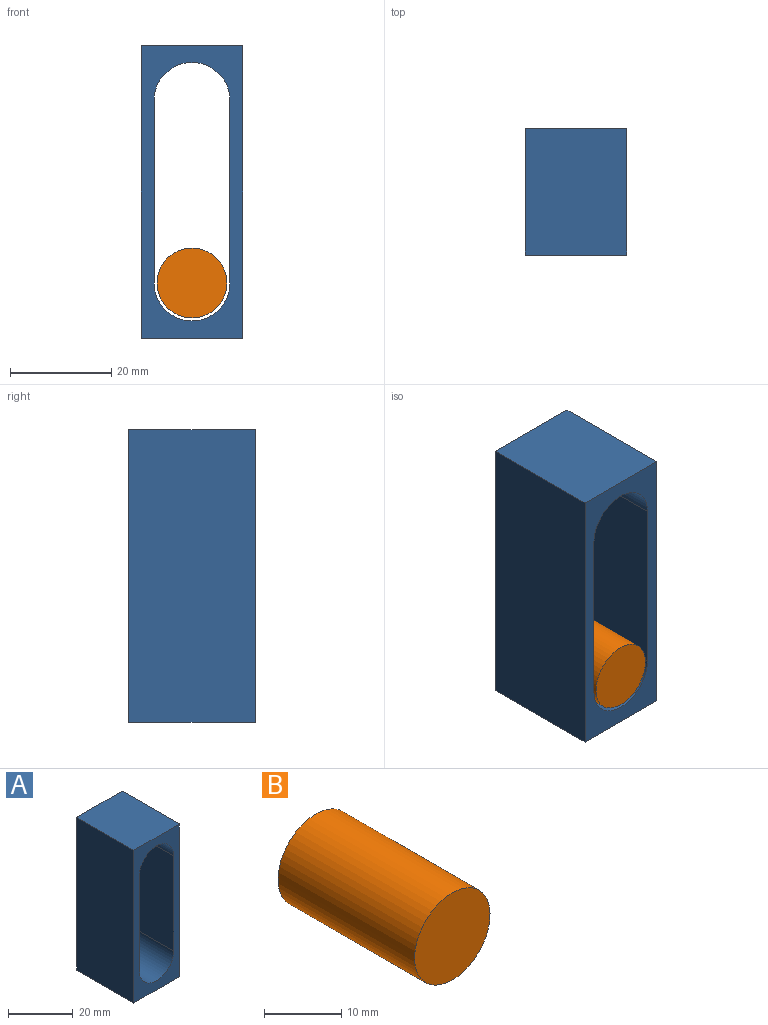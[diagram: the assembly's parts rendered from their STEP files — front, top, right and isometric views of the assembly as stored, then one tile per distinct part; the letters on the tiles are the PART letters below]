
ASSEMBLY  parts=2 mates=1
PART A: 10 faces, bbox 20x25x57.9 mm
  f0: plane 25x19.97mm, normal (0,0,-1), area 499.1mm2, adj f1,f7,f8,f9
  f1: plane 57.85x25mm, normal (1,0,0), area 1446.3mm2, adj f0,f2,f8,f9
  f2: plane 25x19.97mm, normal (0,0,1), area 499.1mm2, adj f1,f7,f8,f9
  f3: plane 36.06x25mm, normal (1,0,0), area 901.6mm2, adj f4,f6,f8,f9
  f4: cylinder r=7.5mm len=25mm, axis (0,1,0), area 589mm2, adj f3,f5,f8,f9
  f5: plane 36.06x25mm, normal (-1,0,0), area 901.6mm2, adj f4,f6,f8,f9
  f6: cylinder r=7.5mm len=25mm, axis (0,1,0), area 589mm2, adj f3,f5,f8,f9
  f7: plane 57.85x25mm, normal (-1,0,0), area 1446.3mm2, adj f0,f2,f8,f9
  f8: plane 57.85x19.97mm, normal (0,-1,0), area 437.3mm2, adj f0,f1,f2,f3,f4,f5,f6,f7
  f9: plane 57.85x19.97mm, normal (0,1,0), area 437.3mm2, adj f0,f1,f2,f3,f4,f5,f6,f7
PART B: 3 faces, bbox 13.8x25x13.8 mm
  f0: cylinder r=6.91mm len=25mm, axis (0,1,0), area 1084.8mm2, adj f1,f2
  f1: plane 13.81x13.81mm, normal (0,-1,0), area 149.8mm2, adj f0
  f2: plane 13.81x13.81mm, normal (0,1,0), area 149.8mm2, adj f0
PLACE A at identity
PLACE B rot(axis=(0,-1,0),90deg) t=(18.09,0,-17.98)mm
MATE pin_slot B.f0 <-> A.f6  axis (0,-1,0) through (0,-25,-17.98)mm
